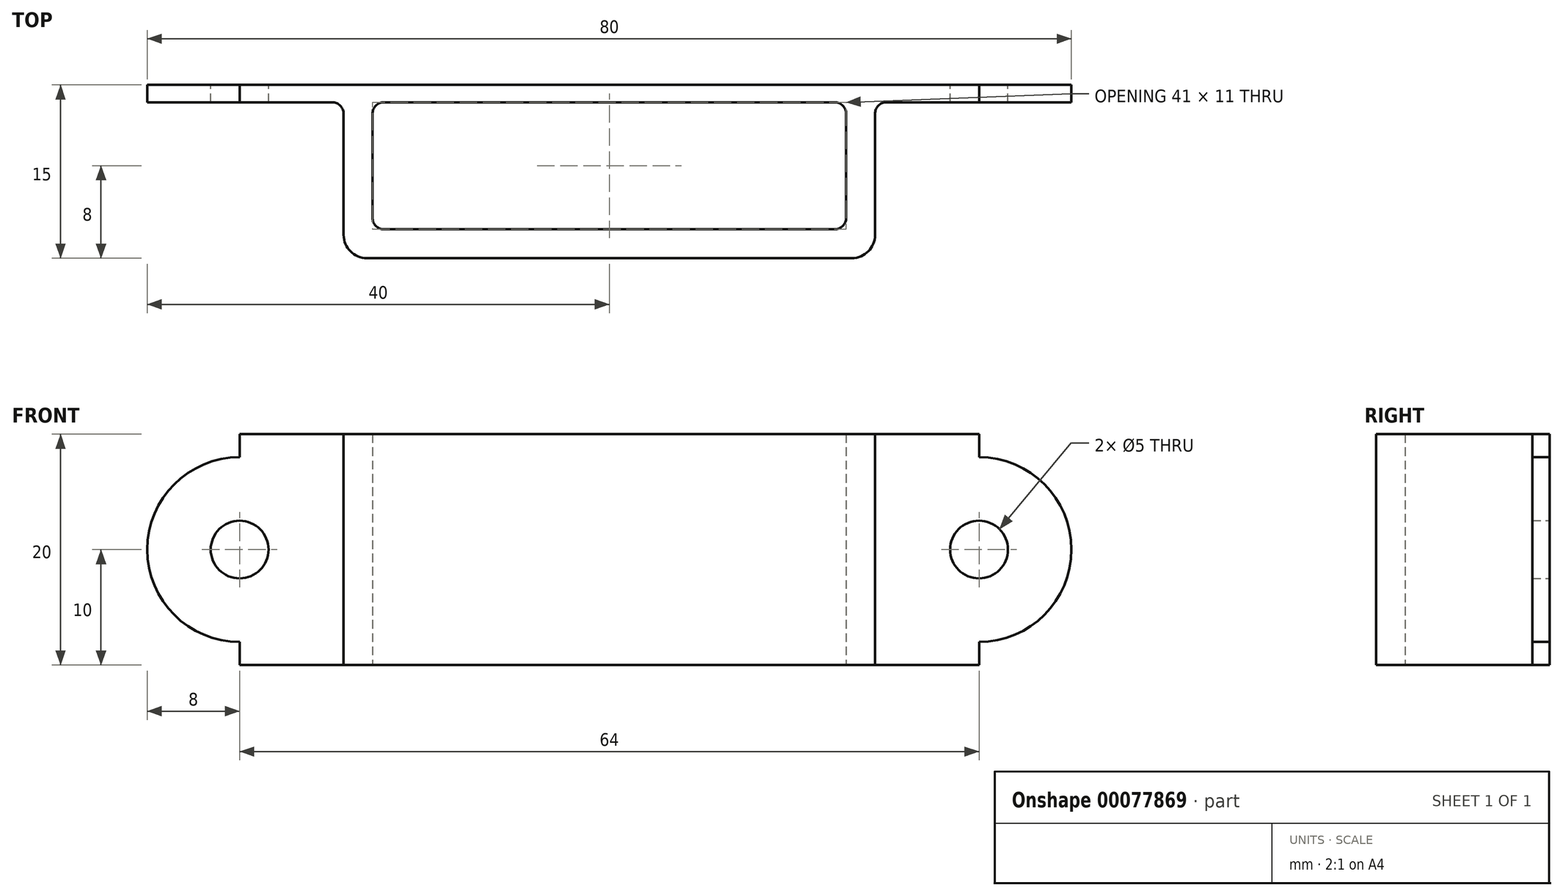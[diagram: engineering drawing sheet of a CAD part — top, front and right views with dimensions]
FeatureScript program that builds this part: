
annotation { "Feature Type Name" : "Feature", "Feature Type Description" : "" }
export const myFeature = defineFeature(function(context is Context, id is Id, definition is map)
    precondition{}
    {
        {
            var Q0;
            Q0=qCreatedBy(makeId("Front.planeOp"),FACE);
            var sketch = newSketch(context, id + "F0", { "sketchPlane" : qUnion([Q0])});
            skLineSegment(sketch, "E0.bottom", {"start": v(-32, 10) * mm, "end": v(32, 10) * mm});
            skLineSegment(sketch, "E0.top", {"start": v(-32, -10) * mm, "end": v(32, -10) * mm});
            skLineSegment(sketch, "E0.left", {"start": v(-32, 10) * mm, "end": v(-32, -10) * mm});
            skLineSegment(sketch, "E0.right", {"start": v(32, 10) * mm, "end": v(32, -10) * mm});
            skArc(sketch, "E1", {"start": v(-32, 8) * mm, "mid": v(-40, 0) * mm, "end": v(-32, -8) * mm});
            skLineSegment(sketch, "E2", {"start": v(-23, 10) * mm, "end": v(-23, -10) * mm});
            skLineSegment(sketch, "E3", {"start": v(23, 10) * mm, "end": v(23, -10) * mm});
            skLineSegment(sketch, "E4", {"start": v(-23, 0) * mm, "end": v(23, 0) * mm});
            skPoint(sketch, "E5", {"position": v(0, 0) * mm});
            skArc(sketch, "E6.trimOffspring", {"start": v(32, -8) * mm, "mid": v(40, 0) * mm, "end": v(32, 8) * mm});
            skPoint(sketch, "E7", {"position": v(0, 10) * mm});
            skPoint(sketch, "E8", {"position": v(0, -10) * mm});
            skSolve(sketch);
        }
        {
            var Q0;
            {var subQ5=sQuery(id+"F0.wireOp",EDGE,"E4");Q0=makeQuery(id+"F0.imprint","IMPRINT",FACE,{"disambiguationData":[TD([[makeQuery(id+"F0.imprint","IMPRINT",EDGE,{"derivedFrom":subQ5}),-1.0]])]});}
            var Q1;
            {var subQ5=sQuery(id+"F0.wireOp",EDGE,"E4");Q1=makeQuery(id+"F0.imprint","IMPRINT",FACE,{"disambiguationData":[TD([[makeQuery(id+"F0.imprint","IMPRINT",EDGE,{"derivedFrom":subQ5}),1.0]])]});}
            var Q2;
            {var subQ1=sQuery(id+"F0.wireOp",EDGE,"E0.right");var subQ4=sQuery(id+"F0.wireOp",EDGE,"E0.bottom");var subQ5=makeQuery(id+"F0.imprint","INTERSECT",VERTEX,{"derivedFrom":[subQ4,subQ1]});Q2=makeQuery(id+"F0.imprint","IMPRINT",FACE,{"disambiguationData":[TD([[makeQuery(id+"F0.imprint","IMPRINT",EDGE,{"disambiguationData":[TD([[subQ5,1.0]])],"derivedFrom":subQ4}),-1.0]])]});}
            var Q3;
            {var subQ0=sQuery(id+"F0.wireOp",EDGE,"E6.trimOffspring");Q3=makeQuery(id+"F0.imprint","IMPRINT",FACE,{"disambiguationData":[TD([[makeQuery(id+"F0.imprint","IMPRINT",EDGE,{"derivedFrom":subQ0}),1.0]])]});}
            var Q4;
            {var subQ1=sQuery(id+"F0.wireOp",EDGE,"E0.left");var subQ8=sQuery(id+"F0.wireOp",EDGE,"E0.bottom");var subQ9=makeQuery(id+"F0.imprint","INTERSECT",VERTEX,{"derivedFrom":[subQ8,subQ1]});Q4=makeQuery(id+"F0.imprint","IMPRINT",FACE,{"disambiguationData":[TD([[makeQuery(id+"F0.imprint","IMPRINT",EDGE,{"disambiguationData":[TD([[subQ9,-1.0]])],"derivedFrom":subQ8}),-1.0]])]});}
            var Q5;
            {var subQ0=sQuery(id+"F0.wireOp",EDGE,"E1");Q5=makeQuery(id+"F0.imprint","IMPRINT",FACE,{"disambiguationData":[TD([[makeQuery(id+"F0.imprint","IMPRINT",EDGE,{"derivedFrom":subQ0}),1.0]])]});}
            extrude(context, id + "F1", {"entities" : qUnion([Q0, Q1, Q2, Q3, Q4, Q5]), "depth" : 1.5 * mm});
        }
        {
            var Q0;
            {var subQ5=sQuery(id+"F0.wireOp",EDGE,"E4");Q0=makeQuery(id+"F0.imprint","IMPRINT",FACE,{"disambiguationData":[TD([[makeQuery(id+"F0.imprint","IMPRINT",EDGE,{"derivedFrom":subQ5}),-1.0]])]});}
            var Q1;
            {var subQ5=sQuery(id+"F0.wireOp",EDGE,"E4");Q1=makeQuery(id+"F0.imprint","IMPRINT",FACE,{"disambiguationData":[TD([[makeQuery(id+"F0.imprint","IMPRINT",EDGE,{"derivedFrom":subQ5}),1.0]])]});}
            extrude(context, id + "F2", {"entities" : qUnion([Q0, Q1]), "operationType" : NewBodyOperationType.ADD, "depth" : 15 * mm});
        }
        {
            var Q0;
            Q0=qCreatedBy(makeId("Top.planeOp"),FACE);
            var sketch = newSketch(context, id + "F3", { "sketchPlane" : qUnion([Q0])});
            skLineSegment(sketch, "E9.bottom", {"start": v(-20.5, -1.5) * mm, "end": v(20.5, -1.5) * mm});
            skLineSegment(sketch, "E9.top", {"start": v(-20.5, -12.5) * mm, "end": v(20.5, -12.5) * mm});
            skLineSegment(sketch, "E9.left", {"start": v(-20.5, -1.5) * mm, "end": v(-20.5, -12.5) * mm});
            skLineSegment(sketch, "E9.right", {"start": v(20.5, -1.5) * mm, "end": v(20.5, -12.5) * mm});
            skSolve(sketch);
        }
        {
            var Q0;
            Q0=makeQuery(id+"F3.imprint","IMPRINT",FACE,{"disambiguationData":[TD([[makeQuery(id+"F3.imprint","IMPRINT",EDGE,{"derivedFrom":sQuery(id+"F3.wireOp",EDGE,"E9.bottom")}),-1.0]])]});
            extrude(context, id + "F4", {"entities" : qUnion([Q0]), "operationType" : NewBodyOperationType.REMOVE, "endBound" : BoundingType.SYMMETRIC, "depth" : 25 * mm});
        }
        {
            var Q0;
            Q0=sQuery(id+"F0.wireOp",VERTEX,"E1.center");
            var Q1;
            Q1=sQuery(id+"F0.wireOp",VERTEX,"E6.trimOffspring.center");
            var Q2;
            Q2=makeQuery(id+"F1.opExtrude","SWEPT_BODY",BODY,{"disambiguationData":[OSD([sQuery(id+"F0.wireOp",EDGE,"E0.bottom"),sQuery(id+"F0.wireOp",EDGE,"E0.top"),sQuery(id+"F0.wireOp",EDGE,"E0.left"),sQuery(id+"F0.wireOp",EDGE,"E0.right"),sQuery(id+"F0.wireOp",EDGE,"E1"),sQuery(id+"F0.wireOp",EDGE,"E6.trimOffspring")])]});
            hole(context, id + "F5", {"style" : HoleStyle.SIMPLE, "endStyle" : HoleEndStyle.THROUGH, "oppositeDirection" : true, "holeDiameter" : 5 * mm, "locations" : qUnion([Q0, Q1]), "scope" : qUnion([Q2]), "isTappedThrough" : true});
        }
        {
            var Q0;
            Q0=makeQuery(id+"F2.boolean.opBoolean","INTERSECT",EDGE,{"derivedFrom":[makeQuery(id+"F1.opExtrude","CAP_FACE",FACE,{"disambiguationData":[OSD([sQuery(id+"F0.wireOp",EDGE,"E0.bottom"),sQuery(id+"F0.wireOp",EDGE,"E0.top"),sQuery(id+"F0.wireOp",EDGE,"E0.left"),sQuery(id+"F0.wireOp",EDGE,"E0.right"),sQuery(id+"F0.wireOp",EDGE,"E1"),sQuery(id+"F0.wireOp",EDGE,"E6.trimOffspring")])],"isStart":false}),makeQuery(id+"F2.opExtrude","SWEPT_FACE",FACE,{"disambiguationData":[OSD([sQuery(id+"F0.wireOp",EDGE,"E2")])]})]});
            var Q1;
            Q1=makeQuery(id+"F4.boolean.opBoolean","COPY",EDGE,{"derivedFrom":makeQuery(id+"F4.opExtrude","SWEPT_EDGE",EDGE,{"disambiguationData":[OSD([sQuery(id+"F3.wireOp",EDGE,"E9.bottom"),sQuery(id+"F3.wireOp",EDGE,"E9.left")])]})});
            var Q2;
            Q2=makeQuery(id+"F2.boolean.opBoolean","INTERSECT",EDGE,{"derivedFrom":[makeQuery(id+"F1.opExtrude","CAP_FACE",FACE,{"disambiguationData":[OSD([sQuery(id+"F0.wireOp",EDGE,"E0.bottom"),sQuery(id+"F0.wireOp",EDGE,"E0.top"),sQuery(id+"F0.wireOp",EDGE,"E0.left"),sQuery(id+"F0.wireOp",EDGE,"E0.right"),sQuery(id+"F0.wireOp",EDGE,"E1"),sQuery(id+"F0.wireOp",EDGE,"E6.trimOffspring")])],"isStart":false}),makeQuery(id+"F2.opExtrude","SWEPT_FACE",FACE,{"disambiguationData":[OSD([sQuery(id+"F0.wireOp",EDGE,"E3")])]})]});
            var Q3;
            Q3=makeQuery(id+"F4.boolean.opBoolean","COPY",EDGE,{"derivedFrom":makeQuery(id+"F4.opExtrude","SWEPT_EDGE",EDGE,{"disambiguationData":[OSD([sQuery(id+"F3.wireOp",EDGE,"E9.bottom"),sQuery(id+"F3.wireOp",EDGE,"E9.right")])]})});
            var Q4;
            Q4=makeQuery(id+"F4.boolean.opBoolean","COPY",EDGE,{"derivedFrom":makeQuery(id+"F4.opExtrude","SWEPT_EDGE",EDGE,{"disambiguationData":[OSD([sQuery(id+"F3.wireOp",EDGE,"E9.top"),sQuery(id+"F3.wireOp",EDGE,"E9.left")])]})});
            var Q5;
            Q5=makeQuery(id+"F4.boolean.opBoolean","COPY",EDGE,{"derivedFrom":makeQuery(id+"F4.opExtrude","SWEPT_EDGE",EDGE,{"disambiguationData":[OSD([sQuery(id+"F3.wireOp",EDGE,"E9.top"),sQuery(id+"F3.wireOp",EDGE,"E9.right")])]})});
            fillet(context, id + "F6", {"entities" : qUnion([Q0, Q1, Q2, Q3, Q4, Q5]), "radius" : 1 * mm, "tangentPropagation" : true, "allowEdgeOverflow" : false});
        }
        {
            var Q0;
            Q0=makeQuery(id+"F2.opExtrude","CAP_EDGE",EDGE,{"disambiguationData":[OSD([sQuery(id+"F0.wireOp",EDGE,"E2")])],"isStart":false});
            var Q1;
            Q1=makeQuery(id+"F2.opExtrude","CAP_EDGE",EDGE,{"disambiguationData":[OSD([sQuery(id+"F0.wireOp",EDGE,"E3")])],"isStart":false});
            fillet(context, id + "F7", {"entities" : qUnion([Q0, Q1]), "radius" : 2 * mm, "tangentPropagation" : true, "allowEdgeOverflow" : false});
        }
    });
